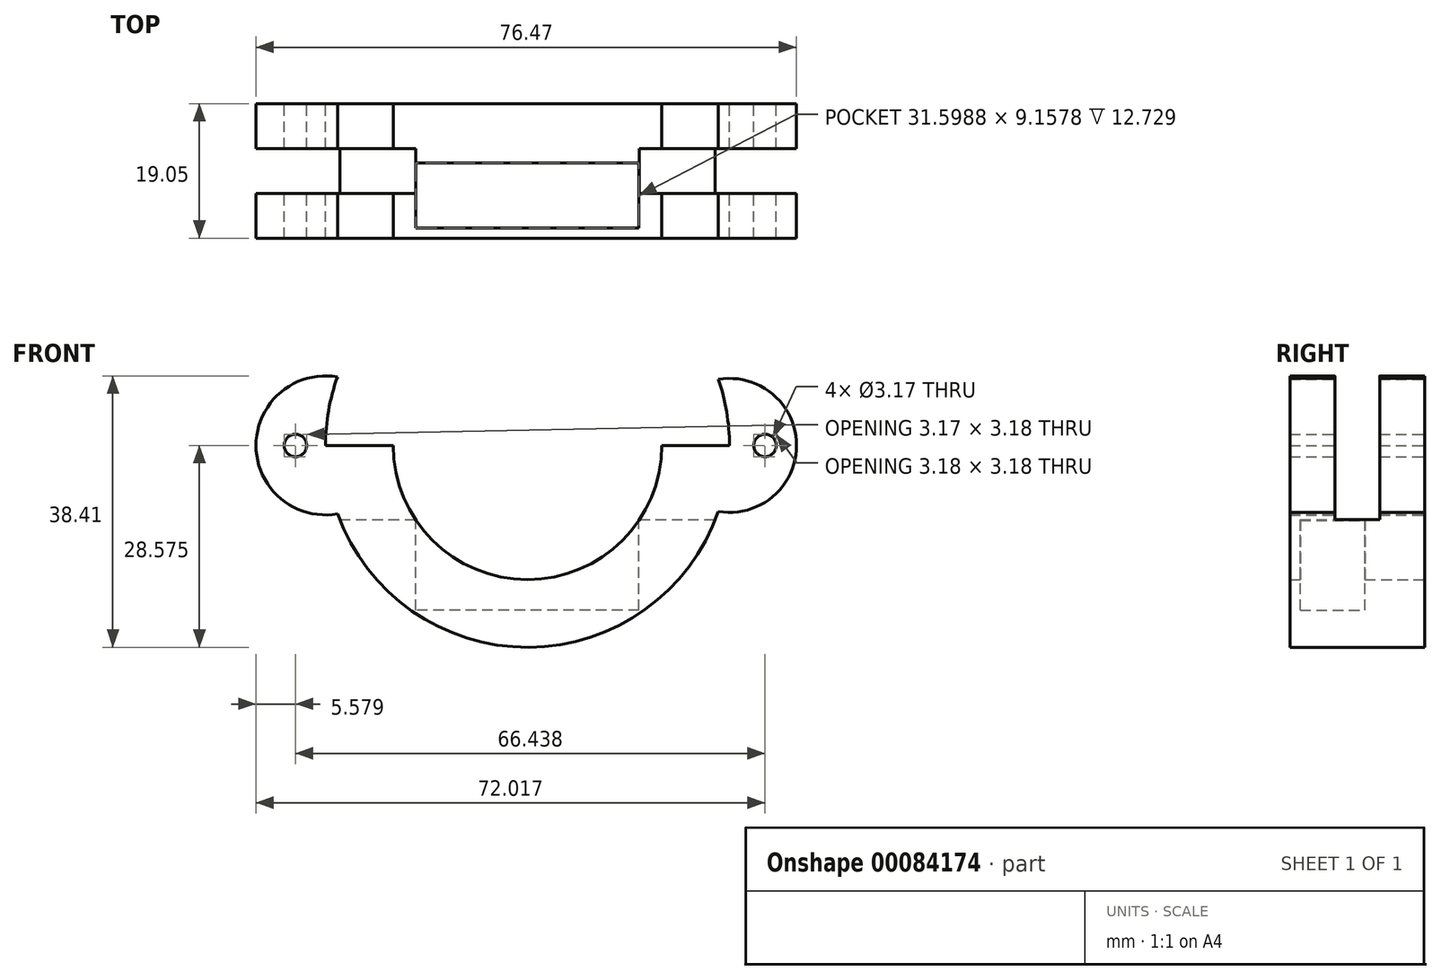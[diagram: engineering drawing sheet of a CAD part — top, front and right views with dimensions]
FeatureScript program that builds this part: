
annotation { "Feature Type Name" : "Feature", "Feature Type Description" : "" }
export const myFeature = defineFeature(function(context is Context, id is Id, definition is map)
    precondition{}
    {
        {
            var Q0;
            Q0=qCreatedBy(makeId("Front.planeOp"),FACE);
            var sketch = newSketch(context, id + "F0", { "sketchPlane" : qUnion([Q0])});
            skArc(sketch, "E0", {"start": v(-34.77, 27.01) * mm, "mid": v(-15.77, 8.01) * mm, "end": v(3.23, 27.01) * mm});
            skArc(sketch, "E1", {"start": v(-42.65, 36.7) * mm, "mid": v(-43.92, 31.93) * mm, "end": v(-44.34, 27.01) * mm});
            skArc(sketch, "E2", {"start": v(-42.65, 36.7) * mm, "mid": v(-54.18, 27.01) * mm, "end": v(-42.65, 17.32) * mm});
            skArc(sketch, "E3", {"start": v(11.23, 17.66) * mm, "mid": v(22.29, 27.01) * mm, "end": v(11.23, 36.37) * mm});
            skCircle(sketch, "E4", {"center": v(-48.6, 27.01) * mm, "radius": 1.59 * mm});
            skPoint(sketch, "E4.centerSnap0", {"position": v(-54.18, 27.01) * mm});
            skCircle(sketch, "E5", {"center": v(17.84, 27.01) * mm, "radius": 1.59 * mm});
            skLineSegment(sketch, "E6", {"start": v(-44.34, 27.01) * mm, "end": v(-34.77, 27.01) * mm});
            skLineSegment(sketch, "E7", {"start": v(3.23, 27.01) * mm, "end": v(12.8, 27.01) * mm});
            skArc(sketch, "E8.trimOffspring", {"start": v(-42.65, 17.32) * mm, "mid": v(-15.59, -1.56) * mm, "end": v(11.23, 17.66) * mm});
            skArc(sketch, "E9.trimOffspring", {"start": v(12.8, 27.01) * mm, "mid": v(12.4, 31.76) * mm, "end": v(11.23, 36.37) * mm});
            skSolve(sketch);
        }
        {
            var Q0;
            Q0 = qSketchRegion(id + "F0", true);
            extrude(context, id + "F1", {"entities" : qUnion([Q0]), "depth" : 19.05 * mm});
        }
        {
            var Q0;
            Q0=qCreatedBy(makeId("Right.planeOp"),FACE);
            var sketch = newSketch(context, id + "F2", { "sketchPlane" : qUnion([Q0])});
            skLineSegment(sketch, "E10", {"start": v(-6.35, 16.5) * mm, "end": v(-12.7, 16.5) * mm});
            skLineSegment(sketch, "E11", {"start": v(-6.35, 16.5) * mm, "end": v(-6.35, 38.39) * mm});
            skLineSegment(sketch, "E12", {"start": v(-12.7, 16.5) * mm, "end": v(-12.7, 38.39) * mm});
            skLineSegment(sketch, "E13", {"start": v(-12.7, 38.39) * mm, "end": v(-6.35, 38.39) * mm});
            skSolve(sketch);
        }
        {
            var Q0;
            Q0 = qSketchRegion(id + "F2", true);
            extrude(context, id + "F3", {"entities" : qUnion([Q0]), "operationType" : NewBodyOperationType.REMOVE, "oppositeDirection" : true, "depth" : 69.31 * mm, "hasSecondDirection" : true, "secondDirectionOppositeDirection" : false, "secondDirectionDepth" : 25.4 * mm});
        }
        {
            var Q0;
            {var subQ1=sQuery(id+"F0.wireOp",EDGE,"E6");Q0=makeQuery(id+"F3.boolean.opBoolean","SPLIT",FACE,{"disambiguationData":[TD([makeQuery(id+"F3.opExtrude","SWEPT_FACE",FACE,{"disambiguationData":[OSD([sQuery(id+"F2.wireOp",EDGE,"E12")])]})])],"derivedFrom":makeQuery(id+"F1.opExtrude","SWEPT_FACE",FACE,{"disambiguationData":[OSD([subQ1])]})});}
            var Q1;
            Q1=makeQuery(id+"F1.opExtrude","CAP_VERTEX",VERTEX,{"disambiguationData":[OSD([sQuery(id+"F0.wireOp",EDGE,"E1"),sQuery(id+"F0.wireOp",EDGE,"E2")])],"isStart":false});
            cPlane(context, id + "F4", {"entities" : qUnion([Q0, Q1]), "cplaneType" : CPlaneType.PLANE_POINT, "offset" : 38.1 * mm, "width" : 152.4 * mm, "height" : 152.4 * mm});
        }
        {
            var Q0;
            Q0=qCreatedBy(id+"F4.planeOp",FACE);
            var sketch = newSketch(context, id + "F5", { "sketchPlane" : qUnion([Q0])});
            skLineSegment(sketch, "E14.bottom", {"start": v(0, -17.59) * mm, "end": v(-31.6, -17.59) * mm});
            skLineSegment(sketch, "E14.top", {"start": v(0, -8.43) * mm, "end": v(-31.6, -8.43) * mm});
            skLineSegment(sketch, "E14.left", {"start": v(0, -17.59) * mm, "end": v(0, -8.43) * mm});
            skLineSegment(sketch, "E14.right", {"start": v(-31.6, -17.59) * mm, "end": v(-31.6, -8.43) * mm});
            skPoint(sketch, "E14.middle", {"position": v(-15.8, -13) * mm});
            skSolve(sketch);
        }
        {
            var Q0;
            Q0 = qSketchRegion(id + "F5", true);
            extrude(context, id + "F6", {"entities" : qUnion([Q0]), "operationType" : NewBodyOperationType.REMOVE, "oppositeDirection" : true, "depth" : 33.02 * mm});
        }
    });
